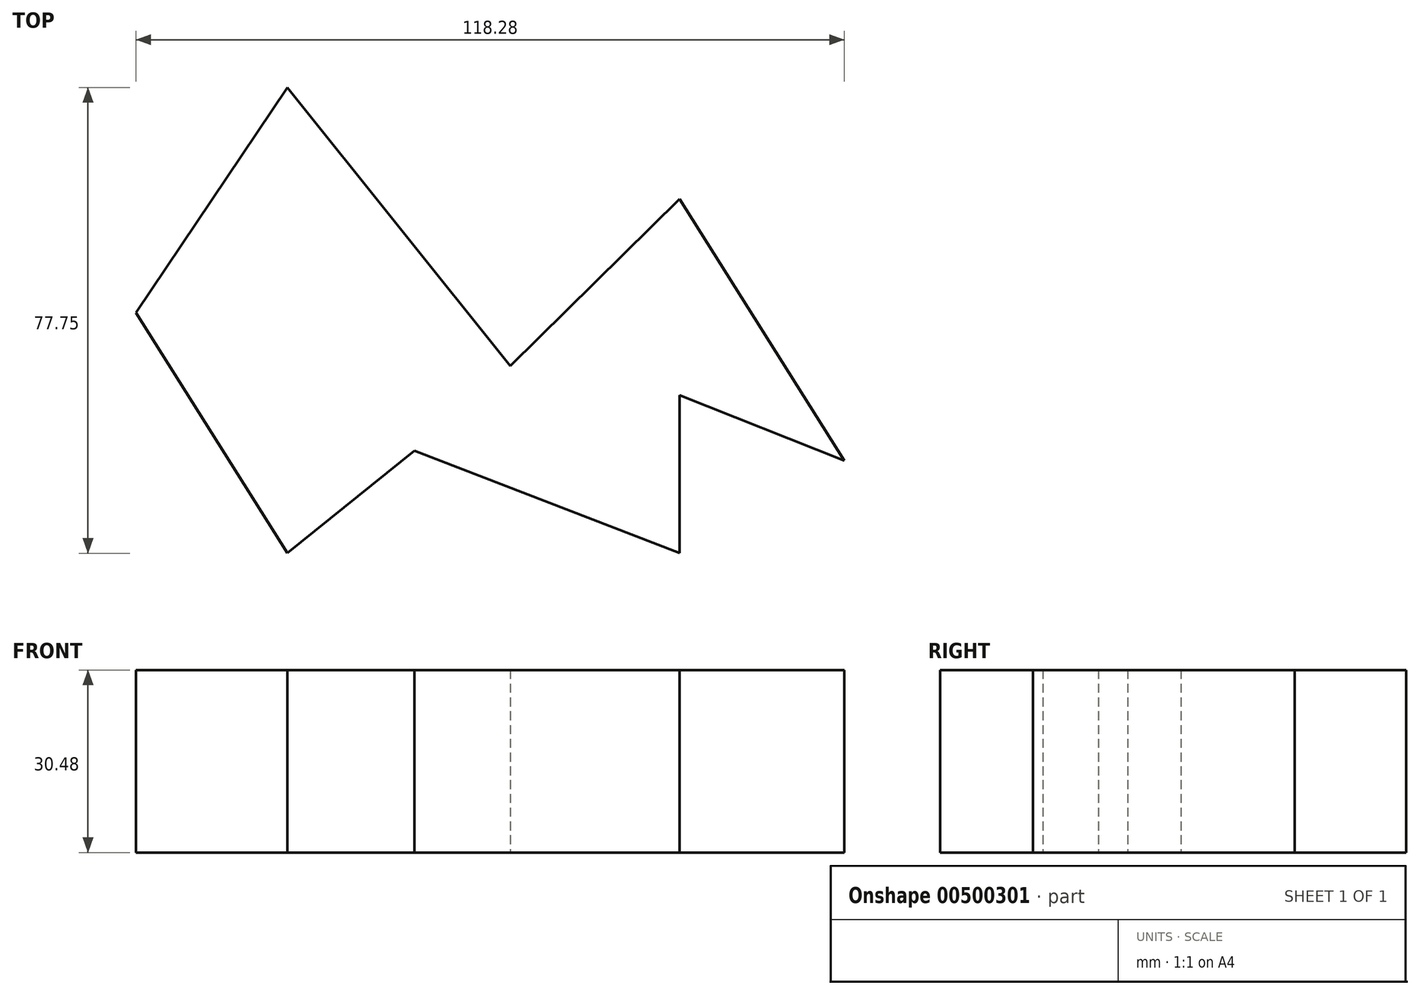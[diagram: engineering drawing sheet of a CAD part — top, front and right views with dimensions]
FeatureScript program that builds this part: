
annotation { "Feature Type Name" : "Feature", "Feature Type Description" : "" }
export const myFeature = defineFeature(function(context is Context, id is Id, definition is map)
    precondition{}
    {
        {
            var Q0;
            Q0=qCreatedBy(makeId("Top.planeOp"),FACE);
            var sketch = newSketch(context, id + "F0", { "sketchPlane" : qUnion([Q0])});
            skLineSegment(sketch, "E0", {"start": v(0, 0) * mm, "end": v(-37.2, 46.47) * mm});
            skLineSegment(sketch, "E1", {"start": v(-37.2, 46.47) * mm, "end": v(-62.5, 8.9) * mm});
            skLineSegment(sketch, "E2", {"start": v(-62.5, 8.9) * mm, "end": v(-37.2, -31.28) * mm});
            skLineSegment(sketch, "E3", {"start": v(-37.2, -31.28) * mm, "end": v(-16, -14.17) * mm});
            skLineSegment(sketch, "E4", {"start": v(0, 0) * mm, "end": v(28.27, 27.87) * mm});
            skLineSegment(sketch, "E5", {"start": v(28.27, 27.87) * mm, "end": v(55.79, -15.84) * mm});
            skLineSegment(sketch, "E6", {"start": v(55.79, -15.84) * mm, "end": v(28.27, -4.87) * mm});
            skLineSegment(sketch, "E7", {"start": v(-16, -14.17) * mm, "end": v(28.27, -31.28) * mm});
            skLineSegment(sketch, "E8", {"start": v(28.27, -4.87) * mm, "end": v(28.27, -31.28) * mm});
            skSolve(sketch);
        }
        {
            var Q0;
            Q0=makeQuery(id+"F0.imprint","IMPRINT",FACE,{"disambiguationData":[TD([[makeQuery(id+"F0.imprint","IMPRINT",EDGE,{"derivedFrom":sQuery(id+"F0.wireOp",EDGE,"E0")}),1.0]])]});
            extrude(context, id + "F1", {"entities" : qUnion([Q0]), "depth" : 30.48 * mm});
        }
    });
